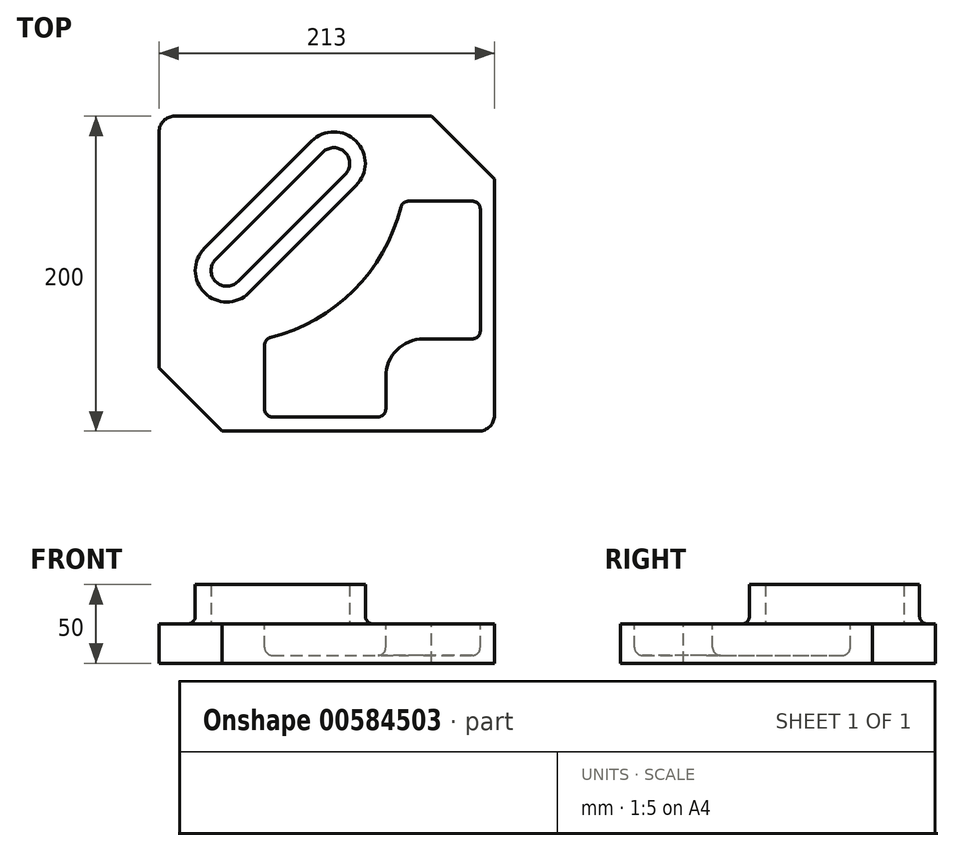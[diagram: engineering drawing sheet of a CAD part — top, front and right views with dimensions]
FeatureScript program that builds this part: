
annotation { "Feature Type Name" : "Feature", "Feature Type Description" : "" }
export const myFeature = defineFeature(function(context is Context, id is Id, definition is map)
    precondition{}
    {
        {
            var Q0;
            Q0=qCreatedBy(makeId("Top.planeOp"),FACE);
            var sketch = newSketch(context, id + "F0", { "sketchPlane" : qUnion([Q0])});
            skLineSegment(sketch, "E0.bottom", {"start": v(0, 0) * mm, "end": v(-213, 0) * mm});
            skLineSegment(sketch, "E0.top", {"start": v(0, 200) * mm, "end": v(-213, 200) * mm});
            skLineSegment(sketch, "E0.left", {"start": v(0, 0) * mm, "end": v(0, 200) * mm});
            skLineSegment(sketch, "E0.right", {"start": v(-213, 0) * mm, "end": v(-213, 200) * mm});
            skSolve(sketch);
        }
        {
            var Q0;
            Q0 = qSketchRegion(id + "F0", true);
            extrude(context, id + "F1", {"entities" : qUnion([Q0]), "depth" : 25 * mm, "offsetDistance" : 25 * mm});
        }
        {
            var Q0;
            Q0=makeQuery(id+"F1.opExtrude","CAP_FACE",FACE,{"disambiguationData":[OSD([sQuery(id+"F0.wireOp",EDGE,"E0.bottom"),sQuery(id+"F0.wireOp",EDGE,"E0.top"),sQuery(id+"F0.wireOp",EDGE,"E0.left"),sQuery(id+"F0.wireOp",EDGE,"E0.right")])],"isStart":false});
            var sketch = newSketch(context, id + "F2", { "sketchPlane" : qUnion([Q0])});
            skLineSegment(sketch, "E1", {"start": v(0, 200) * mm, "end": v(-40, 200) * mm});
            skLineSegment(sketch, "E2", {"start": v(-40, 200) * mm, "end": v(0, 160) * mm});
            skLineSegment(sketch, "E3", {"start": v(0, 160) * mm, "end": v(0, 200) * mm});
            skLineSegment(sketch, "E4", {"start": v(-213, 0) * mm, "end": v(-213, 40) * mm});
            skLineSegment(sketch, "E5", {"start": v(-213, 40) * mm, "end": v(-173, 0) * mm});
            skLineSegment(sketch, "E6", {"start": v(-173, 0) * mm, "end": v(-213, 0) * mm});
            skSolve(sketch);
        }
        {
            var Q0;
            Q0 = qSketchRegion(id + "F2", true);
            extrude(context, id + "F3", {"entities" : qUnion([Q0]), "operationType" : NewBodyOperationType.REMOVE, "oppositeDirection" : true, "depth" : 50 * mm, "offsetDistance" : 25 * mm});
        }
        {
            var Q0;
            Q0=makeQuery(id+"F1.opExtrude","CAP_FACE",FACE,{"disambiguationData":[OSD([sQuery(id+"F0.wireOp",EDGE,"E0.bottom"),sQuery(id+"F0.wireOp",EDGE,"E0.top"),sQuery(id+"F0.wireOp",EDGE,"E0.left"),sQuery(id+"F0.wireOp",EDGE,"E0.right")])],"isStart":false});
            var sketch = newSketch(context, id + "F4", { "sketchPlane" : qUnion([Q0])});
            skLineSegment(sketch, "E7.bottom", {"start": v(0, 0) * mm, "end": v(-170, 0) * mm, "construction": true});
            skLineSegment(sketch, "E7.top", {"start": v(0, 170) * mm, "end": v(-170, 170) * mm, "construction": true});
            skLineSegment(sketch, "E7.left", {"start": v(0, 0) * mm, "end": v(0, 170) * mm, "construction": true});
            skLineSegment(sketch, "E7.right", {"start": v(-170, 0) * mm, "end": v(-170, 170) * mm, "construction": true});
            skLineSegment(sketch, "E8", {"start": v(-170, 102) * mm, "end": v(-102, 170) * mm});
            skArc(sketch, "E9.0.startCap", {"start": v(-155.86, 87.86) * mm, "mid": v(-184.14, 87.86) * mm, "end": v(-184.14, 116.14) * mm});
            skArc(sketch, "E9.0.endCap", {"start": v(-116.14, 184.14) * mm, "mid": v(-87.86, 184.14) * mm, "end": v(-87.86, 155.86) * mm});
            skLineSegment(sketch, "E9.0.left", {"start": v(-184.14, 116.14) * mm, "end": v(-116.14, 184.14) * mm});
            skLineSegment(sketch, "E9.0.right", {"start": v(-155.86, 87.86) * mm, "end": v(-87.86, 155.86) * mm});
            skArc(sketch, "E10.0.startCap", {"start": v(-162.93, 94.93) * mm, "mid": v(-177.07, 94.93) * mm, "end": v(-177.07, 109.07) * mm});
            skArc(sketch, "E10.0.endCap", {"start": v(-109.07, 177.07) * mm, "mid": v(-94.93, 177.07) * mm, "end": v(-94.93, 162.93) * mm});
            skLineSegment(sketch, "E10.0.left", {"start": v(-177.07, 109.07) * mm, "end": v(-109.07, 177.07) * mm});
            skLineSegment(sketch, "E10.0.right", {"start": v(-162.93, 94.93) * mm, "end": v(-94.93, 162.93) * mm});
            skPoint(sketch, "E11", {"position": v(-146, 58.55) * mm});
            skArc(sketch, "E12", {"start": v(-142.22, 59.44) * mm, "mid": v(-89.39, 89.39) * mm, "end": v(-59.44, 142.22) * mm});
            skPoint(sketch, "E13", {"position": v(-58.55, 146) * mm});
            skLineSegment(sketch, "E14", {"start": v(-146, 54.59) * mm, "end": v(-146, 14) * mm});
            skLineSegment(sketch, "E15", {"start": v(-141, 9) * mm, "end": v(-74, 9) * mm});
            skLineSegment(sketch, "E16", {"start": v(-69, 14) * mm, "end": v(-69, 34.55) * mm});
            skLineSegment(sketch, "E17", {"start": v(-45, 58.55) * mm, "end": v(-14, 58.55) * mm});
            skLineSegment(sketch, "E18", {"start": v(-9, 63.55) * mm, "end": v(-9, 141) * mm});
            skLineSegment(sketch, "E19", {"start": v(-14, 146) * mm, "end": v(-54.59, 146) * mm});
            skPoint(sketch, "E20.visualSharp", {"position": v(-69, 58.55) * mm});
            skArc(sketch, "E20.filletArc", {"start": v(-45, 58.55) * mm, "mid": v(-61.97, 51.53) * mm, "end": v(-69, 34.55) * mm});
            skPoint(sketch, "E21.visualSharp", {"position": v(-146, 9) * mm});
            skArc(sketch, "E21.filletArc", {"start": v(-146, 14) * mm, "mid": v(-144.54, 10.46) * mm, "end": v(-141, 9) * mm});
            skPoint(sketch, "E22.visualSharp", {"position": v(-69, 9) * mm});
            skArc(sketch, "E22.filletArc", {"start": v(-74, 9) * mm, "mid": v(-70.46, 10.46) * mm, "end": v(-69, 14) * mm});
            skArc(sketch, "E23.filletArc", {"start": v(-142.22, 59.44) * mm, "mid": v(-144.94, 57.66) * mm, "end": v(-146, 54.59) * mm});
            skArc(sketch, "E24.filletArc", {"start": v(-54.59, 146) * mm, "mid": v(-57.66, 144.94) * mm, "end": v(-59.44, 142.22) * mm});
            skPoint(sketch, "E25.visualSharp", {"position": v(-9, 146) * mm});
            skArc(sketch, "E25.filletArc", {"start": v(-9, 141) * mm, "mid": v(-10.46, 144.54) * mm, "end": v(-14, 146) * mm});
            skPoint(sketch, "E26.visualSharp", {"position": v(-9, 58.55) * mm});
            skArc(sketch, "E26.filletArc", {"start": v(-14, 58.55) * mm, "mid": v(-10.46, 60.02) * mm, "end": v(-9, 63.55) * mm});
            skSolve(sketch);
        }
        {
            var Q0;
            Q0 = qSketchRegion(id + "F4", true);
            extrude(context, id + "F5", {"entities" : qUnion([Q0]), "operationType" : NewBodyOperationType.ADD, "depth" : 25 * mm, "offsetDistance" : 25 * mm});
        }
        {
            var Q0;
            Q0=makeQuery(id+"F5.opExtrude","CAP_EDGE",EDGE,{"disambiguationData":[OSD([sQuery(id+"F4.wireOp",EDGE,"E9.0.right")])],"isStart":true});
            fillet(context, id + "F6", {"entities" : qUnion([Q0]), "radius" : 5 * mm, "tangentPropagation" : true, "allowEdgeOverflow" : false});
        }
        {
            var Q0;
            Q0=makeQuery(id+"F5.opExtrude","CAP_FACE",FACE,{"disambiguationData":[OSD([sQuery(id+"F4.wireOp",EDGE,"E12"),sQuery(id+"F4.wireOp",EDGE,"E14"),sQuery(id+"F4.wireOp",EDGE,"E15"),sQuery(id+"F4.wireOp",EDGE,"E16"),sQuery(id+"F4.wireOp",EDGE,"E17"),sQuery(id+"F4.wireOp",EDGE,"E18"),sQuery(id+"F4.wireOp",EDGE,"E19"),sQuery(id+"F4.wireOp",EDGE,"E20.filletArc")])],"isStart":false});
            extrude(context, id + "F7", {"entities" : qUnion([Q0]), "operationType" : NewBodyOperationType.REMOVE, "oppositeDirection" : true, "depth" : 45 * mm, "offsetDistance" : 25 * mm});
        }
        {
            var Q0;
            Q0=makeQuery(id+"F5.opExtrude","CAP_EDGE",EDGE,{"disambiguationData":[OSD([sQuery(id+"F4.wireOp",EDGE,"E14")])],"isStart":true});
            var Q1;
            Q1=makeQuery(id+"F7.boolean.opBoolean","COPY",EDGE,{"derivedFrom":makeQuery(id+"F7.opExtrude","CAP_EDGE",EDGE,{"disambiguationData":[OSD([sQuery(id+"F4.wireOp",EDGE,"E12")])],"isStart":false})});
            fillet(context, id + "F8", {"entities" : qUnion([Q0, Q1]), "radius" : 5 * mm, "tangentPropagation" : true, "allowEdgeOverflow" : false});
        }
        {
            var Q0;
            Q0=makeQuery(id+"F1.opExtrude","SWEPT_EDGE",EDGE,{"disambiguationData":[OSD([sQuery(id+"F0.wireOp",EDGE,"E0.bottom"),sQuery(id+"F0.wireOp",EDGE,"E0.left")])]});
            var Q1;
            Q1=makeQuery(id+"F1.opExtrude","SWEPT_EDGE",EDGE,{"disambiguationData":[OSD([sQuery(id+"F0.wireOp",EDGE,"E0.top"),sQuery(id+"F0.wireOp",EDGE,"E0.right")])]});
            fillet(context, id + "F9", {"entities" : qUnion([Q0, Q1]), "radius" : 10 * mm, "tangentPropagation" : true, "allowEdgeOverflow" : false});
        }
    });
